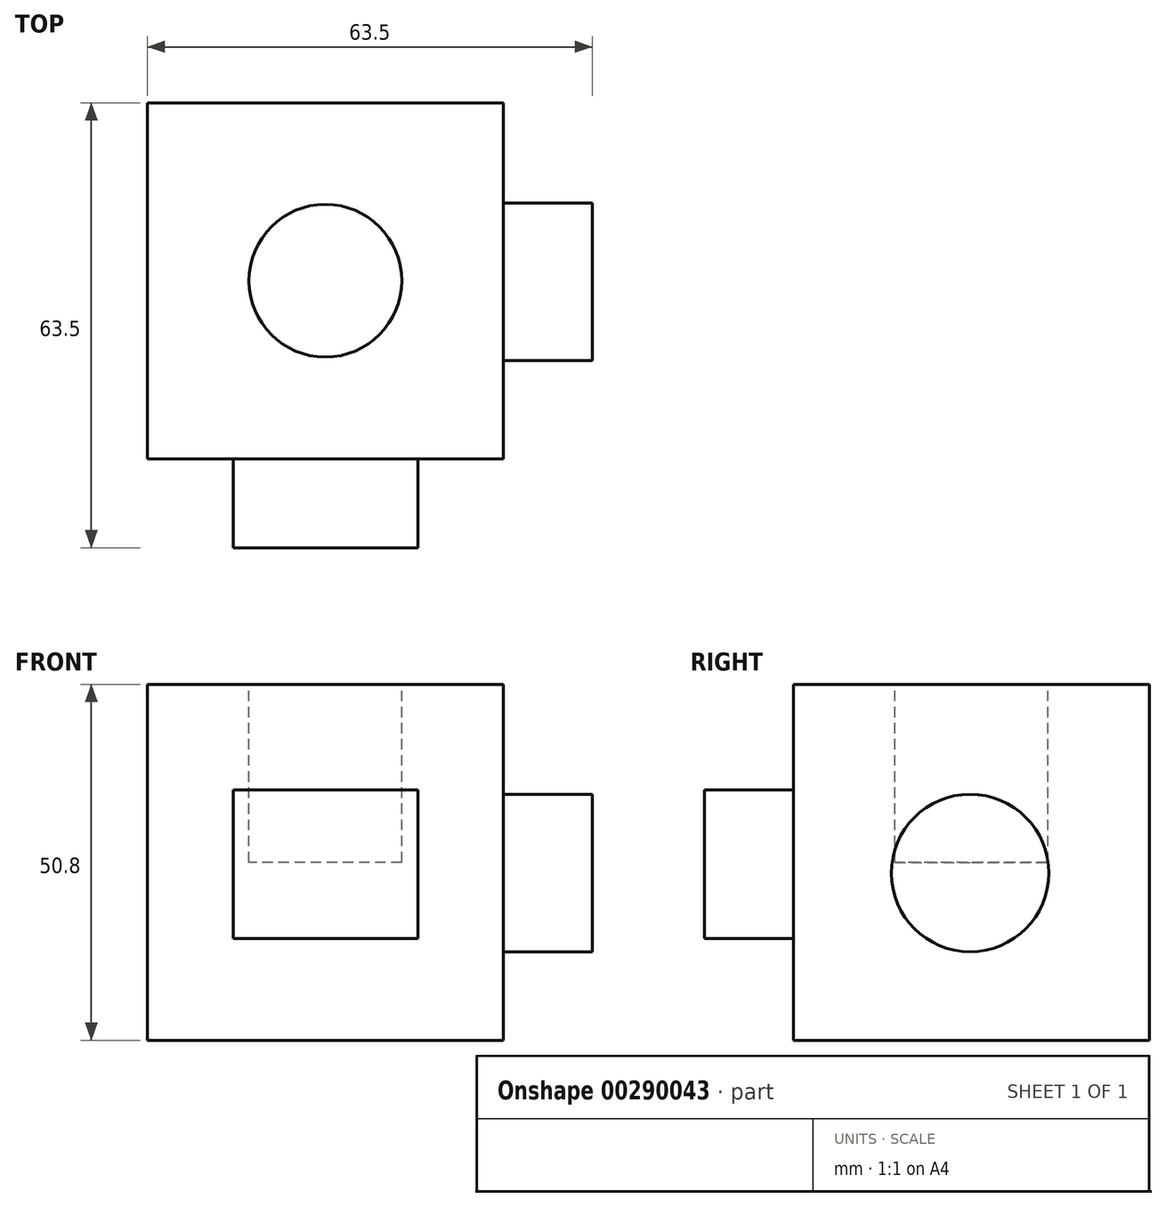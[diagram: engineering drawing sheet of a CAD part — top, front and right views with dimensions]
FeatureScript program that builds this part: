
annotation { "Feature Type Name" : "Feature", "Feature Type Description" : "" }
export const myFeature = defineFeature(function(context is Context, id is Id, definition is map)
    precondition{}
    {
        {
            var Q0;
            Q0=qCreatedBy(makeId("Front.planeOp"),FACE);
            var sketch = newSketch(context, id + "F0", { "sketchPlane" : qUnion([Q0])});
            skLineSegment(sketch, "E0", {"start": v(0, 0) * mm, "end": v(-50.8, 0) * mm});
            skLineSegment(sketch, "E1", {"start": v(-50.8, 0) * mm, "end": v(-50.8, 50.8) * mm});
            skLineSegment(sketch, "E2", {"start": v(-50.8, 50.8) * mm, "end": v(0, 50.8) * mm});
            skLineSegment(sketch, "E3", {"start": v(0, 50.8) * mm, "end": v(0, 0) * mm});
            skSolve(sketch);
        }
        {
            var Q0;
            Q0=makeQuery(id+"F0.imprint","IMPRINT",FACE,{"disambiguationData":[TD([[makeQuery(id+"F0.imprint","IMPRINT",EDGE,{"derivedFrom":sQuery(id+"F0.wireOp",EDGE,"E0")}),-1.0]])]});
            extrude(context, id + "F1", {"entities" : qUnion([Q0]), "depth" : 50.8 * mm});
        }
        {
            var Q0;
            Q0=makeQuery(id+"F1.opExtrude","SWEPT_FACE",FACE,{"disambiguationData":[OSD([sQuery(id+"F0.wireOp",EDGE,"E2")])]});
            var sketch = newSketch(context, id + "F2", { "sketchPlane" : qUnion([Q0])});
            skCircle(sketch, "E4", {"center": v(-25.4, -25.4) * mm, "radius": 10.9 * mm});
            skSolve(sketch);
        }
        {
            var Q0;
            Q0=makeQuery(id+"F2.imprint","IMPRINT",FACE,{"disambiguationData":[TD([[makeQuery(id+"F2.imprint","IMPRINT",EDGE,{"derivedFrom":sQuery(id+"F2.wireOp",EDGE,"E4")}),1.0]])]});
            extrude(context, id + "F3", {"entities" : qUnion([Q0]), "operationType" : NewBodyOperationType.REMOVE, "oppositeDirection" : true, "depth" : 25.4 * mm});
        }
        {
            var Q0;
            Q0=makeQuery(id+"F1.opExtrude","CAP_FACE",FACE,{"disambiguationData":[OSD([sQuery(id+"F0.wireOp",EDGE,"E0"),sQuery(id+"F0.wireOp",EDGE,"E1"),sQuery(id+"F0.wireOp",EDGE,"E2"),sQuery(id+"F0.wireOp",EDGE,"E3")])],"isStart":false});
            var sketch = newSketch(context, id + "F4", { "sketchPlane" : qUnion([Q0])});
            skLineSegment(sketch, "E5.bottom", {"start": v(-38.1, 38.1) * mm, "end": v(-12.7, 38.1) * mm});
            skLineSegment(sketch, "E5.top", {"start": v(-38.1, 12.7) * mm, "end": v(-12.7, 12.7) * mm});
            skLineSegment(sketch, "E5.left", {"start": v(-38.1, 38.1) * mm, "end": v(-38.1, 12.7) * mm});
            skLineSegment(sketch, "E5.right", {"start": v(-12.7, 38.1) * mm, "end": v(-12.7, 12.7) * mm});
            skSolve(sketch);
        }
        {
            var Q0;
            Q0=makeQuery(id+"F4.imprint","IMPRINT",FACE,{"disambiguationData":[TD([[makeQuery(id+"F4.imprint","IMPRINT",EDGE,{"derivedFrom":sQuery(id+"F4.wireOp",EDGE,"E5.bottom")}),-1.0]])]});
            extrude(context, id + "F5", {"entities" : qUnion([Q0]), "operationType" : NewBodyOperationType.ADD, "depth" : 25.4 * mm});
        }
        {
            var Q0;
            Q0=makeQuery(id+"F5.opExtrude","CAP_FACE",FACE,{"disambiguationData":[OSD([sQuery(id+"F4.wireOp",EDGE,"E5.bottom"),sQuery(id+"F4.wireOp",EDGE,"E5.top"),sQuery(id+"F4.wireOp",EDGE,"E5.left"),sQuery(id+"F4.wireOp",EDGE,"E5.right")])],"isStart":false});
            extrude(context, id + "F6", {"entities" : qUnion([Q0]), "operationType" : NewBodyOperationType.ADD, "depth" : 12.7 * mm});
        }
        {
            var Q0;
            Q0=makeQuery(id+"F6.opExtrude","CAP_FACE",FACE,{"disambiguationData":[OSD([sQuery(id+"F4.wireOp",EDGE,"E5.bottom"),sQuery(id+"F4.wireOp",EDGE,"E5.top"),sQuery(id+"F4.wireOp",EDGE,"E5.left"),sQuery(id+"F4.wireOp",EDGE,"E5.right")])],"isStart":false});
            extrude(context, id + "F7", {"entities" : qUnion([Q0]), "operationType" : NewBodyOperationType.REMOVE, "oppositeDirection" : true, "depth" : 38.1 * mm});
        }
        {
            var Q0;
            Q0=makeQuery(id+"F7.boolean.opBoolean","MERGE",FACE,{"derivedFrom":[makeQuery(id+"F1.opExtrude","CAP_FACE",FACE,{"disambiguationData":[OSD([sQuery(id+"F0.wireOp",EDGE,"E0"),sQuery(id+"F0.wireOp",EDGE,"E1"),sQuery(id+"F0.wireOp",EDGE,"E2"),sQuery(id+"F0.wireOp",EDGE,"E3")])],"isStart":false}),makeQuery(id+"F7.opExtrude","CAP_FACE",FACE,{"disambiguationData":[OSD([sQuery(id+"F4.wireOp",EDGE,"E5.bottom"),sQuery(id+"F4.wireOp",EDGE,"E5.top"),sQuery(id+"F4.wireOp",EDGE,"E5.left"),sQuery(id+"F4.wireOp",EDGE,"E5.right")])],"isStart":false})]});
            var sketch = newSketch(context, id + "F8", { "sketchPlane" : qUnion([Q0])});
            skLineSegment(sketch, "E6.bottom", {"start": v(-38.57, 35.7) * mm, "end": v(-12.22, 35.7) * mm});
            skLineSegment(sketch, "E6.top", {"start": v(-38.57, 14.51) * mm, "end": v(-12.22, 14.51) * mm});
            skLineSegment(sketch, "E6.left", {"start": v(-38.57, 35.7) * mm, "end": v(-38.57, 14.51) * mm});
            skLineSegment(sketch, "E6.right", {"start": v(-12.22, 35.7) * mm, "end": v(-12.22, 14.51) * mm});
            skSolve(sketch);
        }
        {
            var Q0;
            Q0=makeQuery(id+"F8.imprint","IMPRINT",FACE,{"disambiguationData":[TD([[makeQuery(id+"F8.imprint","IMPRINT",EDGE,{"derivedFrom":sQuery(id+"F8.wireOp",EDGE,"E6.bottom")}),-1.0]])]});
            extrude(context, id + "F9", {"entities" : qUnion([Q0]), "operationType" : NewBodyOperationType.ADD, "depth" : 12.7 * mm});
        }
        {
            var Q0;
            Q0=makeQuery(id+"F1.opExtrude","SWEPT_FACE",FACE,{"disambiguationData":[OSD([sQuery(id+"F0.wireOp",EDGE,"E3")])]});
            var sketch = newSketch(context, id + "F10", { "sketchPlane" : qUnion([Q0])});
            skCircle(sketch, "E7", {"center": v(-25.59, 23.87) * mm, "radius": 11.24 * mm});
            skSolve(sketch);
        }
        {
            var Q0;
            Q0=makeQuery(id+"F10.imprint","IMPRINT",FACE,{"disambiguationData":[TD([[makeQuery(id+"F10.imprint","IMPRINT",EDGE,{"derivedFrom":sQuery(id+"F10.wireOp",EDGE,"E7")}),1.0]])]});
            extrude(context, id + "F11", {"entities" : qUnion([Q0]), "operationType" : NewBodyOperationType.ADD, "depth" : 12.7 * mm});
        }
    });
